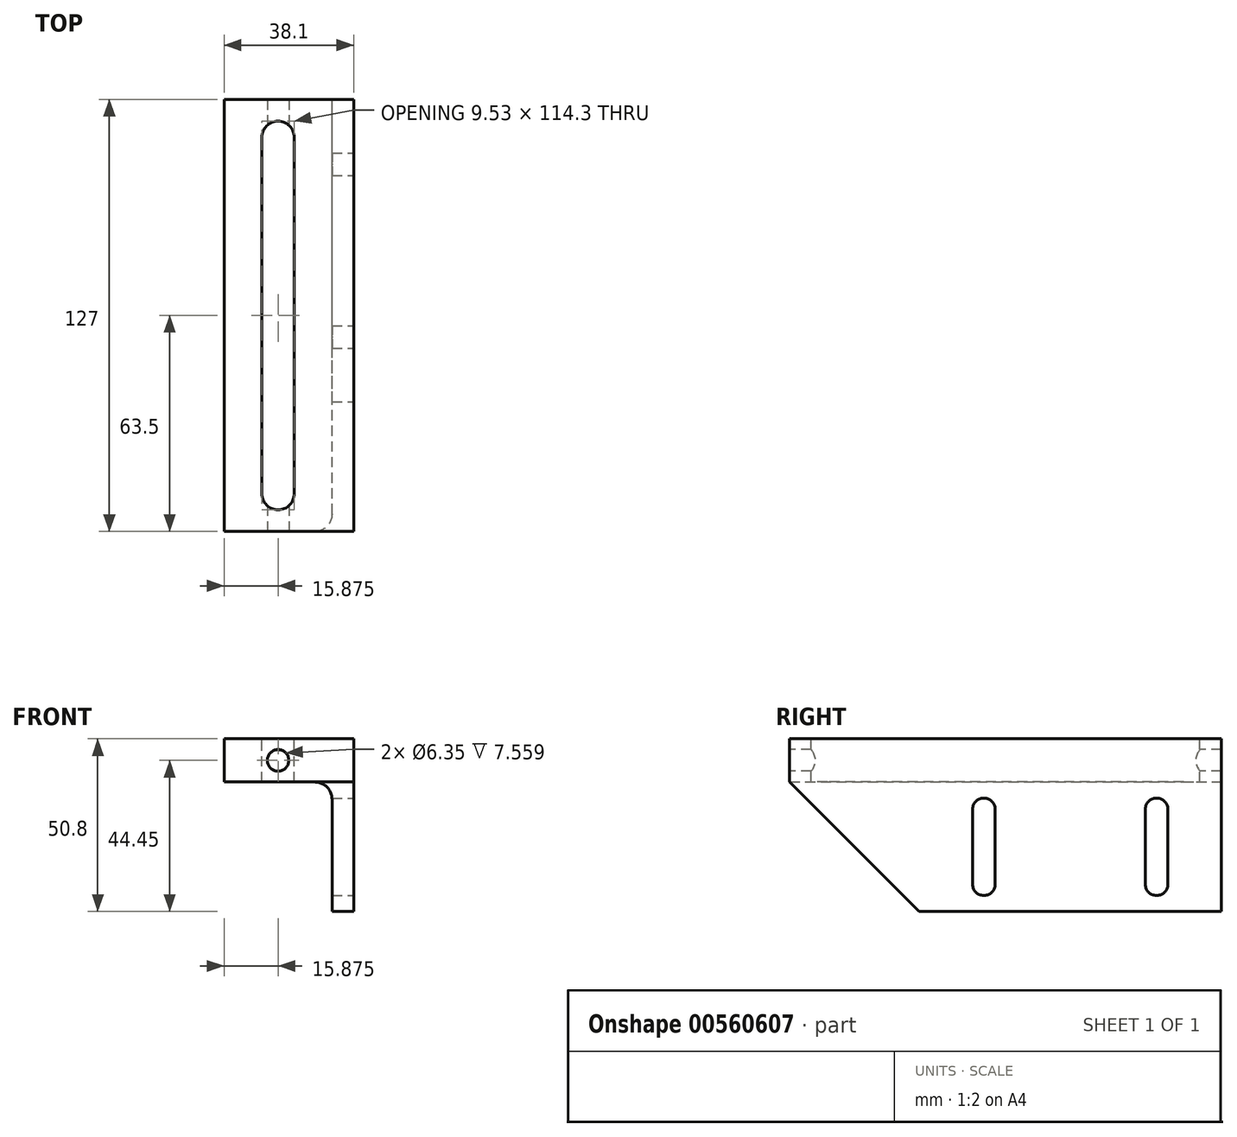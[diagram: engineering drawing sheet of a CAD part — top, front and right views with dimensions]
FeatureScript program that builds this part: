
annotation { "Feature Type Name" : "Feature", "Feature Type Description" : "" }
export const myFeature = defineFeature(function(context is Context, id is Id, definition is map)
    precondition{}
    {
        {
            var Q0;
            Q0=qCreatedBy(makeId("Front.planeOp"),FACE);
            var sketch = newSketch(context, id + "F0", { "sketchPlane" : qUnion([Q0])});
            skLineSegment(sketch, "E0.bottom", {"start": v(19.05, 25.4) * mm, "end": v(-19.05, 25.4) * mm});
            skLineSegment(sketch, "E0.top", {"start": v(19.05, -25.4) * mm, "end": v(12.7, -25.4) * mm});
            skLineSegment(sketch, "E0.left", {"start": v(19.05, 25.4) * mm, "end": v(19.05, -25.4) * mm});
            skLineSegment(sketch, "E0.right", {"start": v(-19.05, 25.4) * mm, "end": v(-19.05, 12.7) * mm});
            skPoint(sketch, "E0.middle", {"position": v(0, 0) * mm});
            skLineSegment(sketch, "E1", {"start": v(-19.05, 12.7) * mm, "end": v(12.7, 12.7) * mm});
            skLineSegment(sketch, "E2", {"start": v(12.7, 12.7) * mm, "end": v(12.7, -25.4) * mm});
            skPoint(sketch, "E3.orphan", {"position": v(-19.05, -25.4) * mm});
            skSolve(sketch);
        }
        {
            var Q0;
            Q0 = qSketchRegion(id + "F0", true);
            extrude(context, id + "F1", {"entities" : qUnion([Q0]), "depth" : 127 * mm, "offsetDistance" : 25.4 * mm});
        }
        {
            var Q0;
            Q0=makeQuery(id+"F1.opExtrude","SWEPT_EDGE",EDGE,{"disambiguationData":[OSD([sQuery(id+"F0.wireOp",EDGE,"E1"),sQuery(id+"F0.wireOp",EDGE,"E2")])]});
            fillet(context, id + "F2", {"entities" : qUnion([Q0]), "radius" : 5.08 * mm, "tangentPropagation" : true, "allowEdgeOverflow" : false});
        }
        {
            var Q0;
            Q0=makeQuery(id+"F1.opExtrude","SWEPT_FACE",FACE,{"disambiguationData":[OSD([sQuery(id+"F0.wireOp",EDGE,"E0.bottom")])]});
            var sketch = newSketch(context, id + "F3", { "sketchPlane" : qUnion([Q0])});
            skLineSegment(sketch, "E4.bottom", {"start": v(-3.19, -6.35) * mm, "end": v(-3.16, -6.35) * mm});
            skLineSegment(sketch, "E4.top", {"start": v(-3.19, -120.65) * mm, "end": v(-3.16, -120.65) * mm});
            skLineSegment(sketch, "E4.left", {"start": v(-7.94, -11.1) * mm, "end": v(-7.94, -115.9) * mm});
            skLineSegment(sketch, "E4.right", {"start": v(1.59, -11.1) * mm, "end": v(1.59, -115.9) * mm});
            skPoint(sketch, "E4.middle", {"position": v(-3.18, -63.5) * mm});
            skPoint(sketch, "E5.visualSharp", {"position": v(1.59, -6.35) * mm});
            skArc(sketch, "E5.filletArc", {"start": v(1.59, -11.1) * mm, "mid": v(0.2, -7.74) * mm, "end": v(-3.16, -6.35) * mm});
            skPoint(sketch, "E6.visualSharp", {"position": v(-7.94, -6.35) * mm});
            skArc(sketch, "E6.filletArc", {"start": v(-3.19, -6.35) * mm, "mid": v(-6.55, -7.74) * mm, "end": v(-7.94, -11.1) * mm});
            skPoint(sketch, "E7.visualSharp", {"position": v(1.59, -120.65) * mm});
            skArc(sketch, "E7.filletArc", {"start": v(-3.16, -120.65) * mm, "mid": v(0.2, -119.26) * mm, "end": v(1.59, -115.9) * mm});
            skPoint(sketch, "E8.visualSharp", {"position": v(-7.94, -120.65) * mm});
            skArc(sketch, "E8.filletArc", {"start": v(-7.94, -115.9) * mm, "mid": v(-6.55, -119.26) * mm, "end": v(-3.19, -120.65) * mm});
            skSolve(sketch);
        }
        {
            var Q0;
            Q0 = qSketchRegion(id + "F3", true);
            extrude(context, id + "F4", {"entities" : qUnion([Q0]), "operationType" : NewBodyOperationType.REMOVE, "endBound" : BoundingType.THROUGH_ALL, "oppositeDirection" : true, "depth" : 25.4 * mm, "offsetDistance" : 25.4 * mm});
        }
        {
            var Q0;
            Q0=makeQuery(id+"F1.opExtrude","CAP_FACE",FACE,{"disambiguationData":[OSD([sQuery(id+"F0.wireOp",EDGE,"E0.bottom"),sQuery(id+"F0.wireOp",EDGE,"E0.top"),sQuery(id+"F0.wireOp",EDGE,"E0.left"),sQuery(id+"F0.wireOp",EDGE,"E0.right"),sQuery(id+"F0.wireOp",EDGE,"E1"),sQuery(id+"F0.wireOp",EDGE,"E2")])],"isStart":false});
            var sketch = newSketch(context, id + "F5", { "sketchPlane" : qUnion([Q0])});
            skCircle(sketch, "E9", {"center": v(-3.18, 19.05) * mm, "radius": 3.18 * mm});
            skPoint(sketch, "E9.centerSnap0", {"position": v(-19.05, 19.05) * mm});
            skSolve(sketch);
        }
        {
            var Q0;
            Q0 = qSketchRegion(id + "F5", true);
            extrude(context, id + "F6", {"entities" : qUnion([Q0]), "operationType" : NewBodyOperationType.REMOVE, "endBound" : BoundingType.THROUGH_ALL, "oppositeDirection" : true, "depth" : 25.4 * mm, "offsetDistance" : 25.4 * mm});
        }
        {
            var Q0;
            Q0=makeQuery(id+"F1.opExtrude","SWEPT_FACE",FACE,{"disambiguationData":[OSD([sQuery(id+"F0.wireOp",EDGE,"E0.left")])]});
            var sketch = newSketch(context, id + "F7", { "sketchPlane" : qUnion([Q0])});
            skLineSegment(sketch, "E10.bottom", {"start": v(-127, -25.4) * mm, "end": v(-88.9, -25.4) * mm});
            skLineSegment(sketch, "E10.left", {"start": v(-127, -25.4) * mm, "end": v(-127, 12.7) * mm});
            skLineSegment(sketch, "E11", {"start": v(-127, 12.7) * mm, "end": v(-88.9, -25.4) * mm});
            skSolve(sketch);
        }
        {
            var Q0;
            Q0 = qSketchRegion(id + "F7", true);
            extrude(context, id + "F8", {"entities" : qUnion([Q0]), "operationType" : NewBodyOperationType.REMOVE, "endBound" : BoundingType.THROUGH_ALL, "oppositeDirection" : true, "depth" : 25.4 * mm, "offsetDistance" : 25.4 * mm});
        }
        {
            var Q0;
            Q0=makeQuery(id+"F1.opExtrude","SWEPT_FACE",FACE,{"disambiguationData":[OSD([sQuery(id+"F0.wireOp",EDGE,"E0.left")])]});
            var sketch = newSketch(context, id + "F9", { "sketchPlane" : qUnion([Q0])});
            skLineSegment(sketch, "E12.bottom", {"start": v(-69.72, 7.94) * mm, "end": v(-69.98, 7.94) * mm});
            skLineSegment(sketch, "E12.top", {"start": v(-69.72, -20.64) * mm, "end": v(-69.98, -20.64) * mm});
            skLineSegment(sketch, "E12.left", {"start": v(-66.55, 4.76) * mm, "end": v(-66.55, -17.46) * mm});
            skLineSegment(sketch, "E12.right", {"start": v(-73.15, 4.76) * mm, "end": v(-73.15, -17.46) * mm});
            skPoint(sketch, "E12.middle", {"position": v(-69.85, -6.35) * mm});
            skLineSegment(sketch, "E13.bottom", {"start": v(-18.92, 7.94) * mm, "end": v(-19.18, 7.94) * mm});
            skLineSegment(sketch, "E13.top", {"start": v(-18.92, -20.64) * mm, "end": v(-19.18, -20.64) * mm});
            skLineSegment(sketch, "E13.left", {"start": v(-15.75, 4.76) * mm, "end": v(-15.75, -17.46) * mm});
            skLineSegment(sketch, "E13.right", {"start": v(-22.35, 4.76) * mm, "end": v(-22.35, -17.46) * mm});
            skPoint(sketch, "E13.middle", {"position": v(-19.05, -6.35) * mm});
            skPoint(sketch, "E13.middle.positionSnap0", {"position": v(-66.55, -6.35) * mm});
            skPoint(sketch, "E13.centerSnap0", {"position": v(-66.55, -6.35) * mm});
            skPoint(sketch, "E14.visualSharp", {"position": v(-66.55, 7.94) * mm});
            skArc(sketch, "E14.filletArc", {"start": v(-66.55, 4.76) * mm, "mid": v(-67.48, 7) * mm, "end": v(-69.72, 7.94) * mm});
            skPoint(sketch, "E15.visualSharp", {"position": v(-73.15, 7.94) * mm});
            skArc(sketch, "E15.filletArc", {"start": v(-69.98, 7.94) * mm, "mid": v(-72.22, 7) * mm, "end": v(-73.15, 4.76) * mm});
            skPoint(sketch, "E16.visualSharp", {"position": v(-66.55, -20.64) * mm});
            skArc(sketch, "E16.filletArc", {"start": v(-69.72, -20.64) * mm, "mid": v(-67.48, -19.7) * mm, "end": v(-66.55, -17.46) * mm});
            skPoint(sketch, "E17.visualSharp", {"position": v(-73.15, -20.64) * mm});
            skArc(sketch, "E17.filletArc", {"start": v(-73.15, -17.46) * mm, "mid": v(-72.22, -19.7) * mm, "end": v(-69.98, -20.64) * mm});
            skPoint(sketch, "E18.visualSharp", {"position": v(-22.35, 7.94) * mm});
            skArc(sketch, "E18.filletArc", {"start": v(-19.18, 7.94) * mm, "mid": v(-21.42, 7) * mm, "end": v(-22.35, 4.76) * mm});
            skPoint(sketch, "E19.visualSharp", {"position": v(-15.75, 7.94) * mm});
            skArc(sketch, "E19.filletArc", {"start": v(-15.75, 4.76) * mm, "mid": v(-16.68, 7) * mm, "end": v(-18.92, 7.94) * mm});
            skPoint(sketch, "E20.visualSharp", {"position": v(-22.35, -20.64) * mm});
            skArc(sketch, "E20.filletArc", {"start": v(-22.35, -17.46) * mm, "mid": v(-21.42, -19.7) * mm, "end": v(-19.18, -20.64) * mm});
            skPoint(sketch, "E21.visualSharp", {"position": v(-15.75, -20.64) * mm});
            skArc(sketch, "E21.filletArc", {"start": v(-18.92, -20.64) * mm, "mid": v(-16.68, -19.7) * mm, "end": v(-15.75, -17.46) * mm});
            skSolve(sketch);
        }
        {
            var Q0;
            Q0 = qSketchRegion(id + "F9", true);
            extrude(context, id + "F10", {"entities" : qUnion([Q0]), "operationType" : NewBodyOperationType.REMOVE, "endBound" : BoundingType.THROUGH_ALL, "oppositeDirection" : true, "depth" : 25.4 * mm, "offsetDistance" : 25.4 * mm});
        }
    });
